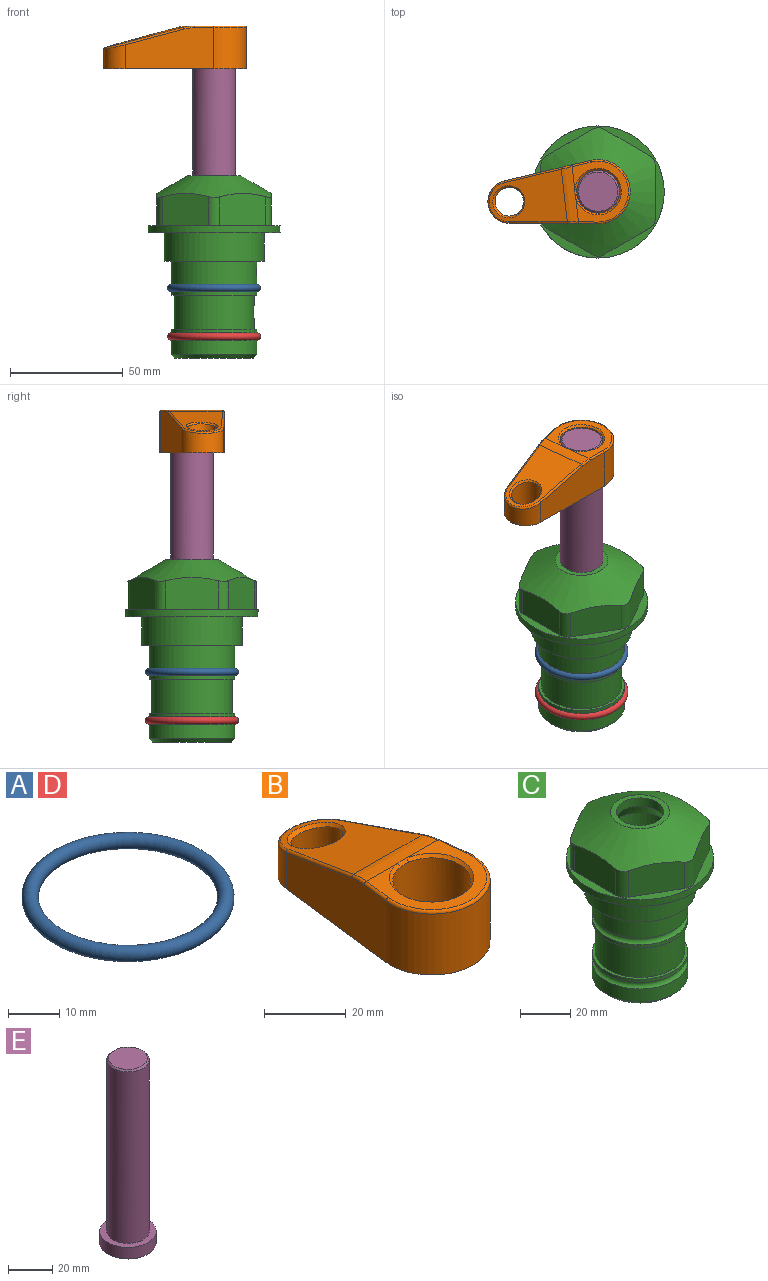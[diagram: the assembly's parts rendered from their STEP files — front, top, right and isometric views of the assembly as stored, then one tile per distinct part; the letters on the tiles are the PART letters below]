
ASSEMBLY  parts=5 mates=4
PART A: 1 faces, bbox 44.7x44.7x3.2 mm
  f0: torus R=19.05mm, axis (0,0,1), area 1193.9mm2
PART B: 31 faces, bbox 31.7x65.5x19.8 mm
  f0: plane 39.12x18.26mm, normal (0.99,0.12,0), area 612.2mm2, adj f1,f4,f7,f11,f13,f15
  f1: cylinder r=9.53mm len=18.91mm, axis (0,0,-1), area 296.1mm2, adj f0,f2,f7,f17
  f2: plane 39.12x18.26mm, normal (-0.99,0.12,0), area 612.2mm2, adj f1,f4,f7,f12,f14,f16
  f3: cylinder r=6.35mm len=12.7mm, axis (0,0,-1), area 362.4mm2, adj f7,f18
  f4: cylinder r=14.29mm len=28.58mm, axis (0,0,-1), area 882.2mm2, adj f0,f2,f7,f10
  f5: cylinder r=9.53mm len=19.05mm, axis (0,0,-1), area 1092.6mm2, adj f7,f19,f20
  f6: plane 26.99x23.69mm, normal (0,0,1), area 216.2mm2, adj f9,f10,f11,f12,f19
  f7: plane 63.5x28.58mm, normal (0,0,-1), area 661.8mm2, adj f0,f1,f2,f3,f4,f5,f22,f23
  f8: plane 33.52x23.6mm, normal (0,0.26,0.97), area 486mm2, adj f9,f15,f16,f17,f18
  f9: cylinder r=19.05mm len=24.72mm, axis (1,0,0), area 120.4mm2, adj f6,f8,f13,f14,f20
  f10: torus R=13.49mm, axis (0,0,1), area 59mm2, adj f4,f6,f11,f12
  f11: cylinder r=0.79mm len=8.67mm, axis (0.12,-0.99,0), area 10.8mm2, adj f0,f6,f10,f13
  f12: cylinder r=0.79mm len=8.67mm, axis (0.12,0.99,0), area 10.8mm2, adj f2,f6,f10,f14
  f13: bspline ~4.95x1.42mm, area 6.1mm2, adj f0,f9,f11,f15
  f14: bspline ~4.95x1.42mm, area 6.1mm2, adj f2,f9,f12,f16
  f15: cylinder r=0.79mm len=25.95mm, axis (0.12,-0.96,0.26), area 32.9mm2, adj f0,f8,f13,f17
  f16: cylinder r=0.79mm len=25.95mm, axis (0.12,0.96,-0.26), area 32.9mm2, adj f2,f8,f14,f17
  f17: bspline ~18.91x8.38mm, area 30mm2, adj f1,f8,f15,f16
  f18: bspline ~14.29x14.29mm, area 48.3mm2, adj f3,f8
  f19: cone r=9.53mm half-angle=45deg, axis (0,0,1), area 66.5mm2, adj f5,f6,f20
  f20: bspline ~3.22x0.96mm, area 3.5mm2, adj f5,f9,f19
  f21: plane 2.75x2.72mm, normal (0,0,-1), area 2.9mm2, adj f23,f25,f28
  f22: plane 23.05x15.88mm, normal (-0.99,-0.12,0), area 323.6mm2, adj f7,f25,f26,f27,f28,f29
  f23: plane 23.05x15.88mm, normal (0.99,-0.12,0), area 323.6mm2, adj f7,f21,f25,f27,f28,f30
  f24: cylinder r=9.53mm len=10.69mm, axis (0,0,-1), area 114.7mm2, adj f7,f27,f29,f30
  f25: cylinder r=12.7mm len=20.59mm, axis (0,0,-1), area 381.1mm2, adj f7,f21,f22,f23,f26,f28
  f26: plane 2.75x2.72mm, normal (0,0,-1), area 2.9mm2, adj f22,f25,f28
  f27: plane 19.72x18.37mm, normal (0,-0.26,-0.97), area 291.8mm2, adj f22,f23,f24,f28,f29,f30
  f28: cylinder r=15.88mm len=19.92mm, axis (1,0,0), area 54.8mm2, adj f21,f22,f23,f25,f26,f27
  f29: cylinder r=1.59mm len=11mm, axis (0,0,-1), area 34.7mm2, adj f7,f22,f24,f27
  f30: cylinder r=1.59mm len=11mm, axis (0,0,-1), area 34.7mm2, adj f7,f23,f24,f27
PART C: 36 faces, bbox 58.7x58.7x81 mm
  f0: cylinder r=17.78mm len=35.56mm, axis (0,0,1), area 1670.8mm2, adj f23,f24,f31
  f1: cylinder r=19.05mm len=38.1mm, axis (0,0,1), area 1191.9mm2, adj f26,f27,f30
  f2: plane 58.66x58.66mm, normal (0,0,-1), area 1150.6mm2, adj f3,f28
  f3: cylinder r=29.33mm len=58.66mm, axis (0,0,-1), area 585.1mm2, adj f2,f4
  f4: plane 58.66x58.66mm, normal (0,0,1), area 475.9mm2, adj f3,f5,f6,f7,f8,f9,f10,f11
  f5: plane 20.32x14.34mm, normal (-0.5,0.87,0), area 324.4mm2, adj f4,f15,f16,f17
  f6: plane 20.32x14.34mm, normal (0.5,0.87,0), area 324.4mm2, adj f4,f14,f15,f17
  f7: plane 23.48x14.34mm, normal (1,0,0), area 324.4mm2, adj f4,f13,f14,f17
  f8: plane 20.32x14.34mm, normal (0.5,-0.87,0), area 324.4mm2, adj f4,f12,f13,f17
  f9: plane 20.32x14.34mm, normal (-0.5,-0.87,0), area 324.4mm2, adj f4,f11,f12,f17
  f10: plane 23.48x14.34mm, normal (-1,0,0), area 324.4mm2, adj f4,f11,f16,f17
  f11: cylinder r=5.08mm len=12.85mm, axis (0,0,-1), area 67.2mm2, adj f4,f9,f10,f17
  f12: cylinder r=5.08mm len=12.85mm, axis (0,0,-1), area 67.2mm2, adj f4,f8,f9,f17
  f13: cylinder r=5.08mm len=12.85mm, axis (0,0,-1), area 67.2mm2, adj f4,f7,f8,f17
  f14: cylinder r=5.08mm len=12.85mm, axis (0,0,-1), area 67.2mm2, adj f4,f6,f7,f17
  f15: cylinder r=5.08mm len=12.85mm, axis (0,0,-1), area 67.2mm2, adj f4,f5,f6,f17
  f16: cylinder r=5.08mm len=12.85mm, axis (0,0,-1), area 67.2mm2, adj f4,f5,f10,f17
  f17: cone r=11.73mm half-angle=60deg, axis (0,0,-1), area 2071.8mm2, adj f5,f6,f7,f8,f9,f10,f11,f12
  f18: plane 23.46x23.46mm, normal (0,0,1), area 147.4mm2, adj f17,f35
  f19: plane 34.93x34.93mm, normal (0,0,-1), area 958mm2, adj f29
  f20: cylinder r=19.05mm len=38.1mm, axis (0,0,1), area 760.1mm2, adj f21,f29
  f21: torus R=19.05mm, axis (0,0,1), area 565.3mm2, adj f20,f22
  f22: cylinder r=19.05mm len=38.1mm, axis (0,0,1), area 190mm2, adj f21,f23
  f23: plane 38.1x38.1mm, normal (0,0,1), area 146.9mm2, adj f0,f22
  f24: plane 38.1x38.1mm, normal (0,0,-1), area 146.9mm2, adj f0,f25
  f25: cylinder r=19.05mm len=38.1mm, axis (0,0,1), area 190mm2, adj f24,f26
  f26: torus R=19.05mm, axis (0,0,1), area 565.3mm2, adj f1,f25
  f27: plane 44.45x44.45mm, normal (0,0,-1), area 411.7mm2, adj f1,f28
  f28: cylinder r=22.23mm len=44.45mm, axis (0,0,1), area 1773.5mm2, adj f2,f27
  f29: cone r=19.05mm half-angle=45deg, axis (0,0,1), area 257.5mm2, adj f19,f20
  f30: cylinder r=3.17mm len=6.75mm, axis (-1,0,0), area 128mm2, adj f1,f33
  f31: cylinder r=3.17mm len=6.35mm, axis (-1,0,0), area 102.5mm2, adj f0,f33
  f32: plane 25.4x25.4mm, normal (0,0,1), area 506.7mm2, adj f33
  f33: cylinder r=12.7mm len=66.42mm, axis (0,0,-1), area 5236.2mm2, adj f30,f31,f32,f34
  f34: cone r=9.53mm half-angle=30deg, axis (0,0,-1), area 443.4mm2, adj f33,f35
  f35: cylinder r=9.53mm len=19.05mm, axis (0,0,-1), area 240.9mm2, adj f18,f34
PART D: same geometry as A
PART E: 6 faces, bbox 25.4x25.4x101.6 mm
  f0: plane 17.46x17.46mm, normal (0,0,1), area 239.5mm2, adj f5
  f1: plane 25.4x25.4mm, normal (0,0,-1), area 506.7mm2, adj f2
  f2: cylinder r=12.7mm len=25.4mm, axis (0,0,1), area 506.7mm2, adj f1,f3
  f3: plane 25.4x25.4mm, normal (0,0,1), area 221.7mm2, adj f2,f4
  f4: cylinder r=9.53mm len=94.46mm, axis (0,0,1), area 5653mm2, adj f3,f5
  f5: cone r=8.73mm half-angle=45deg, axis (0,0,-1), area 64.4mm2, adj f0,f4
PLACE A at identity
PLACE B rot(axis=(0,0,1),96.5deg) t=(0,0,28.35)mm
PLACE C at identity fixed
PLACE D t=(0,0,-21.59)mm
PLACE E rot(axis=(0,0,1),96.5deg) t=(0,0,27.55)mm
MATE cylindrical C.f0 <-> E.f2  axis (0,0,1) through (0,0,-50.55)mm
MATE fastened C.f0 <-> D.f0  axis (0,0,1) through (0,0,-46.1)mm
MATE fastened A.f0 <-> C.f0  axis (0,0,1) through (0,0,-24.51)mm
MATE fastened E.f2 <-> B.f4  axis (0,0,1) through (0,0,91.05)mm
